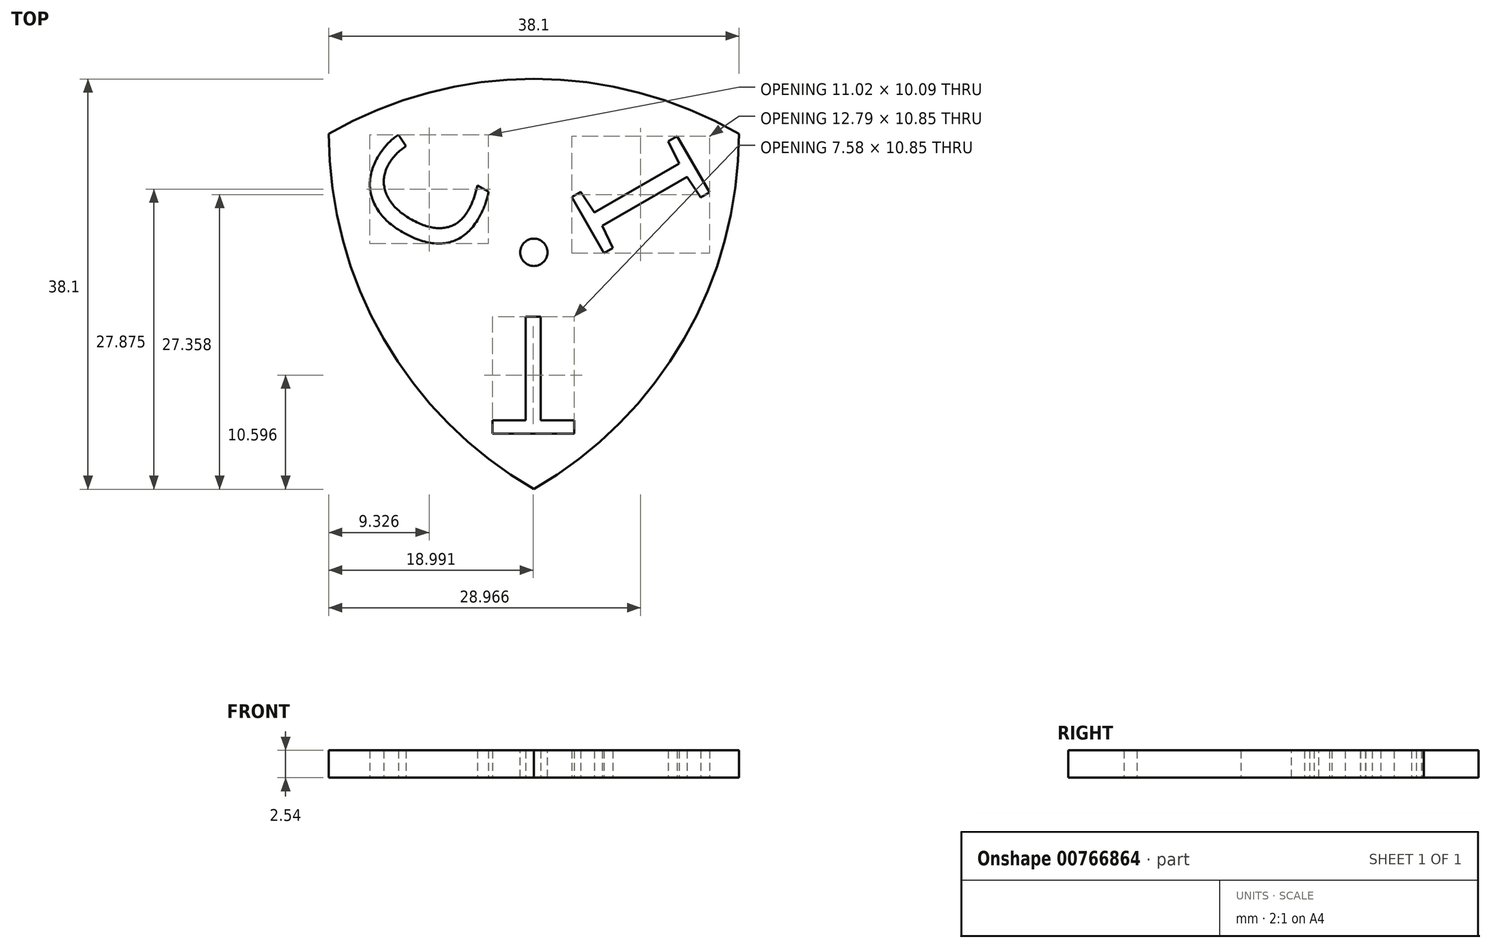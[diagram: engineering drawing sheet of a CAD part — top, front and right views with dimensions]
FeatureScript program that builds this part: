
annotation { "Feature Type Name" : "Feature", "Feature Type Description" : "" }
export const myFeature = defineFeature(function(context is Context, id is Id, definition is map)
    precondition{}
    {
        {
            var Q0;
            Q0=qCreatedBy(makeId("Top.planeOp"),FACE);
            var sketch = newSketch(context, id + "F0", { "sketchPlane" : qUnion([Q0])});
            skCircle(sketch, "E0", {"center": v(0, 0) * mm, "radius": 38.1 * mm});
            skSolve(sketch);
        }
        {
            var Q0;
            Q0=makeQuery(id+"F0.imprint","IMPRINT",FACE,{"disambiguationData":[TD([[makeQuery(id+"F0.imprint","IMPRINT",EDGE,{"derivedFrom":sQuery(id+"F0.wireOp",EDGE,"E0")}),1.0]])]});
            var sketch = newSketch(context, id + "F1", { "sketchPlane" : qUnion([Q0])});
            skCircle(sketch, "E1", {"center": v(-38.1, 0) * mm, "radius": 38.1 * mm});
            skSolve(sketch);
        }
        {
            var Q0;
            Q0=qCreatedBy(makeId("Top.planeOp"),FACE);
            var sketch = newSketch(context, id + "F2", { "sketchPlane" : qUnion([Q0])});
            skCircle(sketch, "E2", {"center": v(-19.05, -33) * mm, "radius": 38.1 * mm});
            skSolve(sketch);
        }
        {
            var Q0;
            Q0 = qSketchRegion(id + "F0", true);
            var Q1;
            Q1 = qSketchRegion(id + "F1", true);
            var Q2;
            Q2 = qSketchRegion(id + "F2", true);
            extrude(context, id + "F3", {"entities" : qUnion([Q0, Q1, Q2]), "depth" : 2.54 * mm, "offsetDistance" : 25.4 * mm});
        }
        {
            var Q0;
            Q0=makeQuery(id+"F3.opExtrude","SWEPT_BODY",BODY,{"disambiguationData":[OSD([sQuery(id+"F0.wireOp",EDGE,"E0")])]});
            var Q1;
            Q1=makeQuery(id+"F3.opExtrude","SWEPT_BODY",BODY,{"disambiguationData":[OSD([sQuery(id+"F1.wireOp",EDGE,"E1")])]});
            var Q2;
            Q2=makeQuery(id+"F3.opExtrude","SWEPT_BODY",BODY,{"disambiguationData":[OSD([sQuery(id+"F2.wireOp",EDGE,"E2")])]});
            booleanBodies(context, id + "F4", {"operationType" : BooleanOperationType.INTERSECTION, "tools" : qUnion([Q0, Q1, Q2])});
        }
        {
            var Q0;
            Q0=makeQuery(id+"F3.opExtrude","CAP_FACE",FACE,{"disambiguationData":[OSD([sQuery(id+"F0.wireOp",EDGE,"E0")])],"isStart":false});
            var sketch = newSketch(context, id + "F5", { "sketchPlane" : qUnion([Q0])});
            skPoint(sketch, "E3", {"position": v(-19.05, -11) * mm});
            skLineSegment(sketch, "E4", {"start": v(0, 0) * mm, "end": v(-33, -19.05) * mm, "construction": true});
            skLineSegment(sketch, "E5", {"start": v(-38.1, 0) * mm, "end": v(-5.1, -19.05) * mm, "construction": true});
            skSolve(sketch);
        }
        {
            var Q0;
            Q0=makeQuery(id+"F5.imprint","IMPRINT",FACE,{"disambiguationData":[TD([[makeQuery(id+"F5.imprint","IMPRINT",EDGE,{"derivedFrom":makeQuery(id+"F3.opExtrude","CAP_EDGE",EDGE,{"disambiguationData":[OSD([sQuery(id+"F0.wireOp",EDGE,"E0")])],"isStart":false})}),1.0]])]});
            var sketch = newSketch(context, id + "F6", { "sketchPlane" : qUnion([Q0])});
            skCircle(sketch, "E6", {"center": v(-19.05, -11) * mm, "radius": 1.27 * mm});
            skSolve(sketch);
        }
        {
            var Q0;
            Q0 = qSketchRegion(id + "F6", true);
            extrude(context, id + "F7", {"entities" : qUnion([Q0]), "operationType" : NewBodyOperationType.REMOVE, "endBound" : BoundingType.UP_TO_NEXT, "oppositeDirection" : true, "depth" : 25.4 * mm, "offsetDistance" : 25.4 * mm});
        }
        {
            var Q0;
            Q0=qCreatedBy(makeId("Top.planeOp"),FACE);
            var sketch = newSketch(context, id + "F8", { "sketchPlane" : qUnion([Q0])});
            skText(sketch, "E7", { "text": "C", "fontName": "DroidSansMono.ttf"});
            skText(sketch, "E8", { "text": "I", "fontName": "DroidSansMono.ttf"});
            skText(sketch, "E9", { "text": "T", "fontName": "DroidSansMono.ttf"});
            const initialGuessF8  = {"E7": [-0.02711, -0.0126, 0.5, 0.86603, 0.01073], "E8": [-0.00187, -0.00692, -0.5, 0.86603, 0.0114], "E9": [-0.01456, -0.01698, -1, 0, 0.01094]};
            skSetInitialGuess(sketch, initialGuessF8);
            skSolve(sketch);
        }
        {
            var Q0;
            Q0 = qSketchRegion(id + "F8", true);
            extrude(context, id + "F9", {"entities" : qUnion([Q0]), "operationType" : NewBodyOperationType.REMOVE, "endBound" : BoundingType.UP_TO_NEXT, "depth" : 25.4 * mm, "offsetDistance" : 25.4 * mm});
        }
    });
